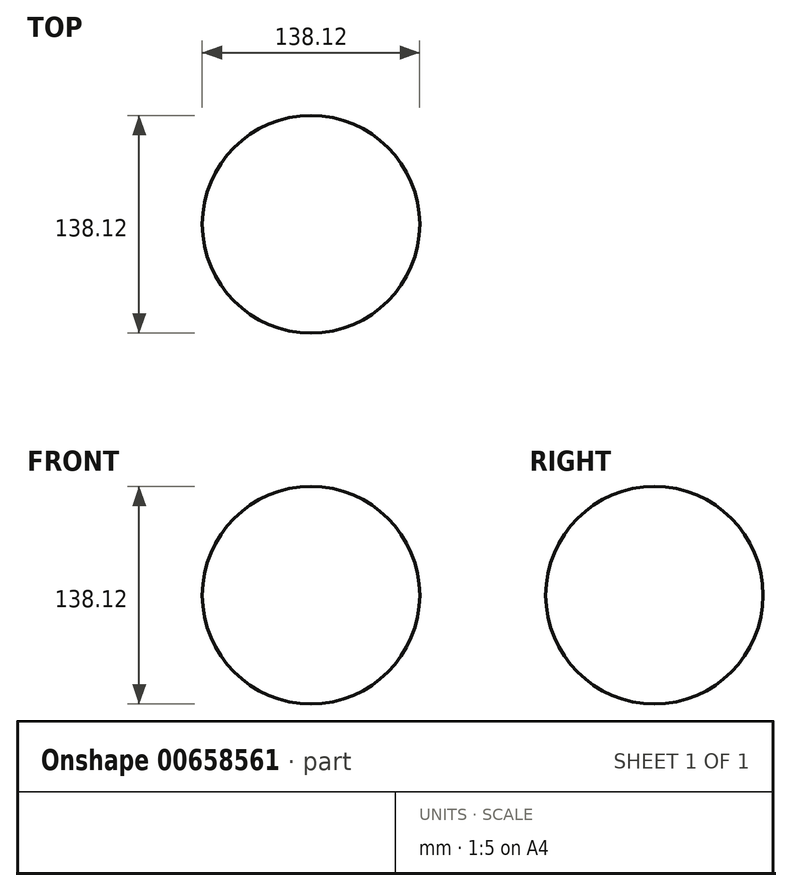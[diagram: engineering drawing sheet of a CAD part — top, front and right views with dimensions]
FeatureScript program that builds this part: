
annotation { "Feature Type Name" : "Feature", "Feature Type Description" : "" }
export const myFeature = defineFeature(function(context is Context, id is Id, definition is map)
    precondition{}
    {
        {
            var Q0;
            Q0=qCreatedBy(makeId("Top.planeOp"),FACE);
            var sketch = newSketch(context, id + "F0", { "sketchPlane" : qUnion([Q0])});
            skArc(sketch, "E0", {"start": v(0, 69.06) * mm, "mid": v(-69.06, 0) * mm, "end": v(0, -69.06) * mm});
            skLineSegment(sketch, "E1", {"start": v(0, 69.06) * mm, "end": v(0, -69.06) * mm});
            skSolve(sketch);
        }
        {
            var Q0;
            Q0=makeQuery(id+"F0.imprint","IMPRINT",FACE,{"disambiguationData":[TD([[makeQuery(id+"F0.imprint","IMPRINT",EDGE,{"derivedFrom":sQuery(id+"F0.wireOp",EDGE,"E0")}),1.0]])]});
            var Q1;
            Q1=sQuery(id+"F0.wireOp",EDGE,"E1");
            revolve(context, id + "F1", {"entities" : qUnion([Q0]), "axis" : qUnion([Q1]), "revolveType" : RevolveType.FULL});
        }
    });
